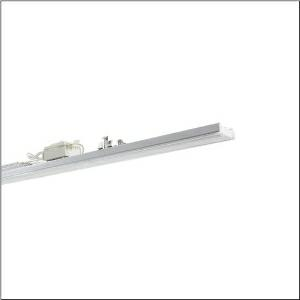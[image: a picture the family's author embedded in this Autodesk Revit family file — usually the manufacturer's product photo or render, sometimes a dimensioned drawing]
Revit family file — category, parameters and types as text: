
# Revit family: licross_r__21_recessed_mo_52tl19dn495g_9489
name_source: partatom
category: Lighting Fixtures
units: mm (PartAtom-declared; Revit-internal decimal feet)

## family parameters
Cut with Voids When Loaded = No
Host = Face
Light Source = No
Part Type = Normal
Room Calculation Point = No
Round Connector Dimension = Use Diameter
Shared = No

## types (1)
- --- (1 x LED, 9850 lm, 58 W, 4000K)
    Apparent Load = 58 VA
    CIE Flux Codes = 55 90 98 100 100
    Color Rendering = 80
    Color Temperature = 4000K
    Default Elevation = 1800 mm
    Description = Licross® 21 Recessed MO, luminaire insert, of sheet steel, galvanised, coil coated, white, length: 1.500mm, width: 66mm, height: 67mm, LED rated luminous flux: 9.850lm, light colour: 840, control gear: DALI 2, with plug, 5-pole, with phase selection, mains connection: 220..240V, AC, 50/60Hz, rated input power: 58W, halogen-free wiring, primary light control with lens, of plastic, primary optical cover: cover, of PMMA, light emission: direct distribution, primary light characteristic: double asymmetric, protection rating (complete): IP40, insulation class (complete): insulation class I (protective earthing), certification: CE, ENEC, VDE, UKCA, protection symbol: D if used in an environment without relevant dust loads with corresponding accessories, impact resistance: IK06, permissible ambient temperature for indoor applications: -25..+35°C, corresponds to IFS (International Featured Standards) requirements for safety and quality in the food industry, reducing of maximum allowable ambient temperature of 5°C with ceiling mounting, LABS conformity tested according to VDMA 24364:2018-05, packaging unit: 1 piece
    Height = 58 mm
    Lamp = 1 x LED
    Lamp Light Flux = 9850 lm
    Lamp Power = 58 W
    Lamp count = 1
    Length = 1500 mm
    Luminous efficacy = 170 lm/W
    Manufacturer = Siteco
    ModVariant = No
    Model = 52TL19DN495G
    Mounting Place = Ceiling
    Mounting Type = Pendant
    Number of Poles = 1
    OnlyDefault = Yes
    Power Factor = 1
    Product Name = Licross® 21 Recessed MO
    Product group = luminaire insert
    ProductGroupID = 902
    Protection Class = Protection class I
    Protection Degree = IP 40
    RLX_Detail_Level = 1
    RLX_Emergency_Light_Flux = 0 lm
    RLX_Emergency_Type = 0
    RLX_Emergency_Type_DB = No
    RlxData = <blob elided: 24585 chars, md5=01c51d08>
    Socket = socket
    Standby Power = 0 W
    System Light Flux = 9850 lm
    System Power = 58 W
    Type Comments = factory setting: luminous flux: 100 % | dim-lin: 254 | 390 mA
    Type Image = l_1296930.jpg
    URL = http://relux.com
    VarID = @adj_127966
    Voltage = 0 V
    Weight = 0.00 kg
    Width = 66 mm

## geometry (parser evidence)
native form markers: Blend x4, Sweep x11
no freeform markers — native parametric forms only
